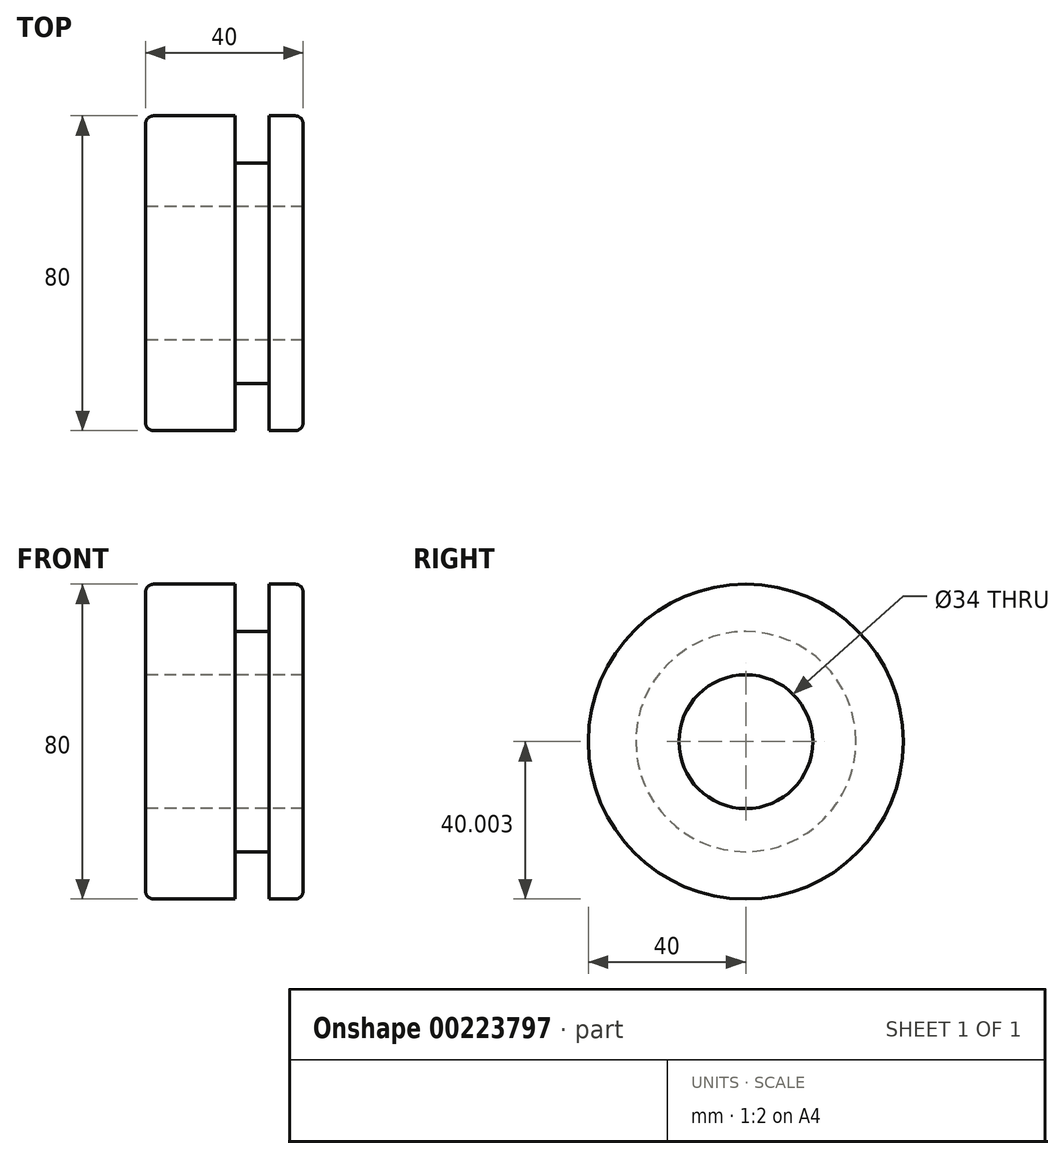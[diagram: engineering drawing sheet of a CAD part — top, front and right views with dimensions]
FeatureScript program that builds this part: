
annotation { "Feature Type Name" : "Feature", "Feature Type Description" : "" }
export const myFeature = defineFeature(function(context is Context, id is Id, definition is map)
    precondition{}
    {
        {
            var Q0;
            Q0=qCreatedBy(makeId("Front.planeOp"),FACE);
            var sketch = newSketch(context, id + "F0", { "sketchPlane" : qUnion([Q0])});
            skLineSegment(sketch, "E0.top", {"start": v(-73.06, -23.57) * mm, "end": v(-33.06, -23.57) * mm});
            skLineSegment(sketch, "E0.left", {"start": v(-73.06, 16.43) * mm, "end": v(-73.06, -23.57) * mm});
            skLineSegment(sketch, "E0.right", {"start": v(-33.06, 16.43) * mm, "end": v(-33.06, -23.57) * mm});
            skLineSegment(sketch, "E1", {"start": v(-73.06, 16.43) * mm, "end": v(-50.32, 16.43) * mm});
            skLineSegment(sketch, "E2", {"start": v(-50.32, 16.43) * mm, "end": v(-50.32, 4.4) * mm});
            skLineSegment(sketch, "E3", {"start": v(-50.32, 4.4) * mm, "end": v(-41.75, 4.4) * mm});
            skLineSegment(sketch, "E4", {"start": v(-41.75, 4.4) * mm, "end": v(-41.75, 16.43) * mm});
            skLineSegment(sketch, "E5", {"start": v(-41.75, 16.43) * mm, "end": v(-33.06, 16.43) * mm});
            skSolve(sketch);
        }
        {
            var Q0;
            Q0 = qSketchRegion(id + "F0", true);
            var Q1;
            Q1=sQuery(id+"F0.wireOp",EDGE,"E0.top");
            revolve(context, id + "F1", {"entities" : qUnion([Q0]), "axis" : qUnion([Q1]), "revolveType" : RevolveType.FULL, "oppositeDirection" : true});
        }
        {
            var Q0;
            Q0=makeQuery(id+"F1.opRevolve","SWEPT_FACE",FACE,{"disambiguationData":[OSD([sQuery(id+"F0.wireOp",EDGE,"E0.right")])]});
            var sketch = newSketch(context, id + "F2", { "sketchPlane" : qUnion([Q0])});
            skCircle(sketch, "E6", {"center": v(0, -23.57) * mm, "radius": 17 * mm});
            skSolve(sketch);
        }
        {
            var Q0;
            Q0=makeQuery(id+"F2.imprint","IMPRINT",FACE,{"disambiguationData":[TD([[makeQuery(id+"F2.imprint","IMPRINT",EDGE,{"derivedFrom":sQuery(id+"F2.wireOp",EDGE,"E6")}),1.0]])]});
            extrude(context, id + "F3", {"entities" : qUnion([Q0]), "operationType" : NewBodyOperationType.REMOVE, "depth" : 254 * mm, "hasDraft" : true, "draftAngle" : 3 * degree, "hasSecondDirection" : true, "secondDirectionBound" : BoundingType.UP_TO_NEXT, "secondDirectionOppositeDirection" : true, "secondDirectionDepth" : 25.4 * mm});
        }
        {
            var Q0;
            Q0=makeQuery(id+"F1.opRevolve","SWEPT_EDGE",EDGE,{"disambiguationData":[OSD([sQuery(id+"F0.wireOp",EDGE,"E0.right"),sQuery(id+"F0.wireOp",EDGE,"E5")])]});
            fillet(context, id + "F4", {"entities" : qUnion([Q0]), "radius" : 2 * mm, "tangentPropagation" : true, "allowEdgeOverflow" : false});
        }
        {
            var Q0;
            Q0=makeQuery(id+"F1.opRevolve","SWEPT_EDGE",EDGE,{"disambiguationData":[OSD([sQuery(id+"F0.wireOp",EDGE,"E0.left"),sQuery(id+"F0.wireOp",EDGE,"E1")])]});
            fillet(context, id + "F5", {"entities" : qUnion([Q0]), "radius" : 2 * mm, "tangentPropagation" : true, "allowEdgeOverflow" : false});
        }
    });
